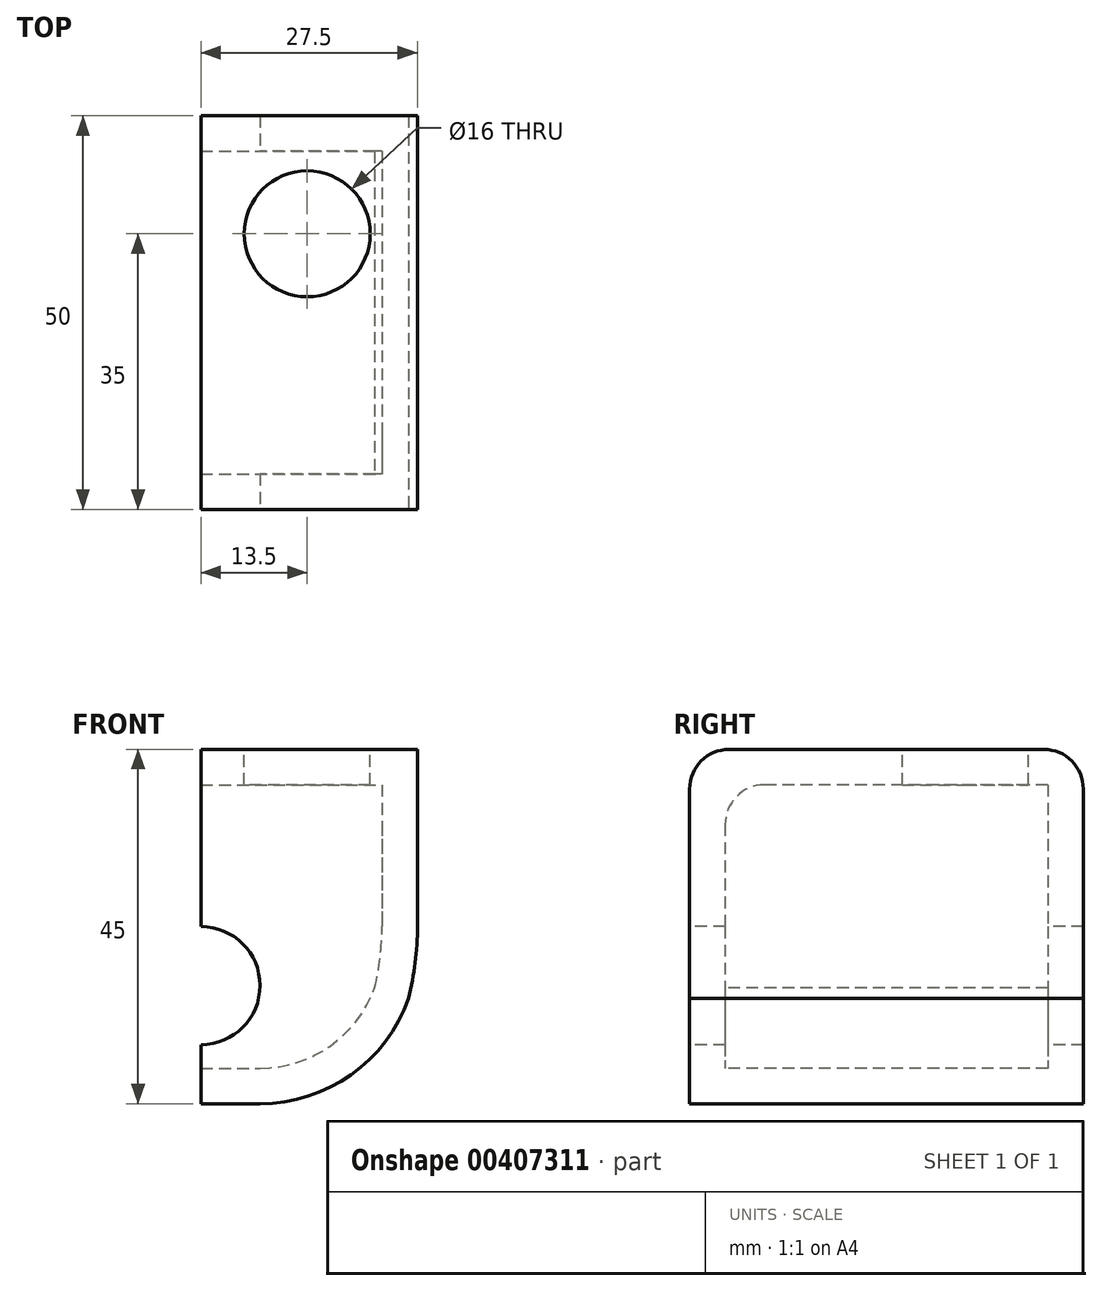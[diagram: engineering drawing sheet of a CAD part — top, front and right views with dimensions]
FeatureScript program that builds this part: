
annotation { "Feature Type Name" : "Feature", "Feature Type Description" : "" }
export const myFeature = defineFeature(function(context is Context, id is Id, definition is map)
    precondition{}
    {
        {
            var Q0;
            Q0=qCreatedBy(makeId("Top.planeOp"),FACE);
            var sketch = newSketch(context, id + "F0", { "sketchPlane" : qUnion([Q0])});
            skLineSegment(sketch, "E0.bottom", {"start": v(0, 0) * mm, "end": v(27.5, 0) * mm});
            skLineSegment(sketch, "E0.top", {"start": v(0, -50) * mm, "end": v(27.5, -50) * mm});
            skLineSegment(sketch, "E0.left", {"start": v(0, 0) * mm, "end": v(0, -50) * mm});
            skLineSegment(sketch, "E0.right", {"start": v(27.5, 0) * mm, "end": v(27.5, -50) * mm});
            skSolve(sketch);
        }
        {
            var Q0;
            Q0 = qSketchRegion(id + "F0", true);
            extrude(context, id + "F1", {"entities" : qUnion([Q0]), "depth" : 45 * mm});
        }
        {
            var Q0;
            Q0=makeQuery(id+"F1.opExtrude","SWEPT_FACE",FACE,{"disambiguationData":[OSD([sQuery(id+"F0.wireOp",EDGE,"E0.top")])]});
            var sketch = newSketch(context, id + "F2", { "sketchPlane" : qUnion([Q0])});
            skLineSegment(sketch, "E1", {"start": v(0, 0) * mm, "end": v(0, 15) * mm});
            skCircle(sketch, "E2", {"center": v(0, 15) * mm, "radius": 7.5 * mm});
            skLineSegment(sketch, "E3", {"start": v(0, 0) * mm, "end": v(20, 0) * mm});
            skLineSegment(sketch, "E4", {"start": v(20, 0) * mm, "end": v(20, 22.5) * mm});
            skPoint(sketch, "E4.endSnap0", {"position": v(0, 22.5) * mm});
            skLineSegment(sketch, "E5", {"start": v(20, 22.5) * mm, "end": v(27.5, 22.5) * mm});
            skLineSegment(sketch, "E6", {"start": v(27.5, 22.5) * mm, "end": v(27.5, 0) * mm});
            skLineSegment(sketch, "E7", {"start": v(27.5, 0) * mm, "end": v(20, 0) * mm});
            skArc(sketch, "E8", {"start": v(20, 0) * mm, "mid": v(25.58, 10.64) * mm, "end": v(27.5, 22.5) * mm});
            skSolve(sketch);
        }
        {
            var Q0;
            Q0=makeQuery(id+"F1.opExtrude","CAP_EDGE",EDGE,{"disambiguationData":[OSD([sQuery(id+"F0.wireOp",EDGE,"E0.right")])],"isStart":true});
            fillet(context, id + "F3", {"entities" : qUnion([Q0]), "radius" : 20 * mm, "tangentPropagation" : true, "allowEdgeOverflow" : false});
        }
        {
            var Q0;
            {var subQ0=sQuery(id+"F2.wireOp",EDGE,"E1");var subQ3=sQuery(id+"F2.wireOp",EDGE,"E2");var subQ4=makeQuery(id+"F2.imprint","INTERSECT",VERTEX,{"derivedFrom":[subQ0,subQ3]});Q0=makeQuery(id+"F2.imprint","IMPRINT",FACE,{"disambiguationData":[TD([[makeQuery(id+"F2.imprint","IMPRINT",EDGE,{"disambiguationData":[TD([[subQ4,1.0]])],"derivedFrom":subQ0}),1.0]])]});}
            var Q1;
            Q1=makeQuery(id+"F2.imprint","IMPRINT",FACE,{"disambiguationData":[TD([[makeQuery(id+"F2.imprint","IMPRINT",EDGE,{"derivedFrom":sQuery(id+"F2.wireOp",EDGE,"E6")}),-1.0]])]});
            extrude(context, id + "F4", {"entities" : qUnion([Q0, Q1]), "operationType" : NewBodyOperationType.REMOVE, "oppositeDirection" : true, "depth" : 50 * mm});
        }
        {
            var Q0;
            {var subQ0=sQuery(id+"F0.wireOp",EDGE,"E0.bottom");var subQ1=sQuery(id+"F0.wireOp",EDGE,"E0.left");var subQ2=sQuery(id+"F0.wireOp",EDGE,"E0.top");Q0=makeQuery(id+"F4.boolean.opBoolean","SPLIT",FACE,{"disambiguationData":[TD([makeQuery(id+"F1.opExtrude","CAP_FACE",FACE,{"disambiguationData":[OSD([subQ0,subQ2,subQ1,sQuery(id+"F0.wireOp",EDGE,"E0.right")])],"isStart":false})])],"derivedFrom":makeQuery(id+"F1.opExtrude","SWEPT_FACE",FACE,{"disambiguationData":[OSD([subQ1])]})});}
            var Q1;
            Q1=makeQuery(id+"F4.boolean.opBoolean","COPY",FACE,{"derivedFrom":makeQuery(id+"F4.opExtrude","SWEPT_FACE",FACE,{"disambiguationData":[OSD([sQuery(id+"F2.wireOp",EDGE,"E2")])]})});
            var Q2;
            {var subQ0=sQuery(id+"F0.wireOp",EDGE,"E0.bottom");var subQ1=sQuery(id+"F0.wireOp",EDGE,"E0.left");var subQ2=sQuery(id+"F0.wireOp",EDGE,"E0.top");Q2=makeQuery(id+"F4.boolean.opBoolean","SPLIT",FACE,{"disambiguationData":[TD([makeQuery(id+"F1.opExtrude","CAP_FACE",FACE,{"disambiguationData":[OSD([subQ0,subQ2,subQ1,sQuery(id+"F0.wireOp",EDGE,"E0.right")])],"isStart":true})])],"derivedFrom":makeQuery(id+"F1.opExtrude","SWEPT_FACE",FACE,{"disambiguationData":[OSD([subQ1])]})});}
            shell(context, id + "F5", {"entities" : qUnion([Q0, Q1, Q2]), "thickness" : 4.5 * mm});
        }
        {
            var Q0;
            Q0=makeQuery(id+"F1.opExtrude","CAP_EDGE",EDGE,{"disambiguationData":[OSD([sQuery(id+"F0.wireOp",EDGE,"E0.top")])],"isStart":false});
            var Q1;
            {var subQ0=sQuery(id+"F0.wireOp",EDGE,"E0.top");Q1=makeQuery(id+"F5.opShell","OFFSET_EDGE",EDGE,{"disambiguationData":[OSD([subQ0]),TDD([makeQuery(id+"F1.opExtrude","CAP_EDGE",EDGE,{"disambiguationData":[OSD([subQ0])],"isStart":false})])]});}
            var Q2;
            Q2=makeQuery(id+"F1.opExtrude","CAP_EDGE",EDGE,{"disambiguationData":[OSD([sQuery(id+"F0.wireOp",EDGE,"E0.bottom")])],"isStart":false});
            fillet(context, id + "F6", {"entities" : qUnion([Q0, Q1, Q2]), "radius" : 5 * mm, "tangentPropagation" : true, "allowEdgeOverflow" : false});
        }
        {
            var Q0;
            Q0=makeQuery(id+"F1.opExtrude","CAP_FACE",FACE,{"disambiguationData":[OSD([sQuery(id+"F0.wireOp",EDGE,"E0.bottom"),sQuery(id+"F0.wireOp",EDGE,"E0.top"),sQuery(id+"F0.wireOp",EDGE,"E0.left"),sQuery(id+"F0.wireOp",EDGE,"E0.right")])],"isStart":false});
            var sketch = newSketch(context, id + "F7", { "sketchPlane" : qUnion([Q0])});
            skLineSegment(sketch, "E9", {"start": v(0, 0) * mm, "end": v(13.5, 0) * mm});
            skLineSegment(sketch, "E10", {"start": v(13.5, 0) * mm, "end": v(13.5, -5) * mm});
            skLineSegment(sketch, "E11", {"start": v(13.5, -5) * mm, "end": v(13.5, -15) * mm});
            skCircle(sketch, "E12", {"center": v(13.5, -15) * mm, "radius": 8 * mm});
            skSolve(sketch);
        }
        {
            var Q0;
            Q0 = qSketchRegion(id + "F7", true);
            extrude(context, id + "F8", {"entities" : qUnion([Q0]), "operationType" : NewBodyOperationType.REMOVE, "oppositeDirection" : true, "depth" : 4.5 * mm});
        }
    });
